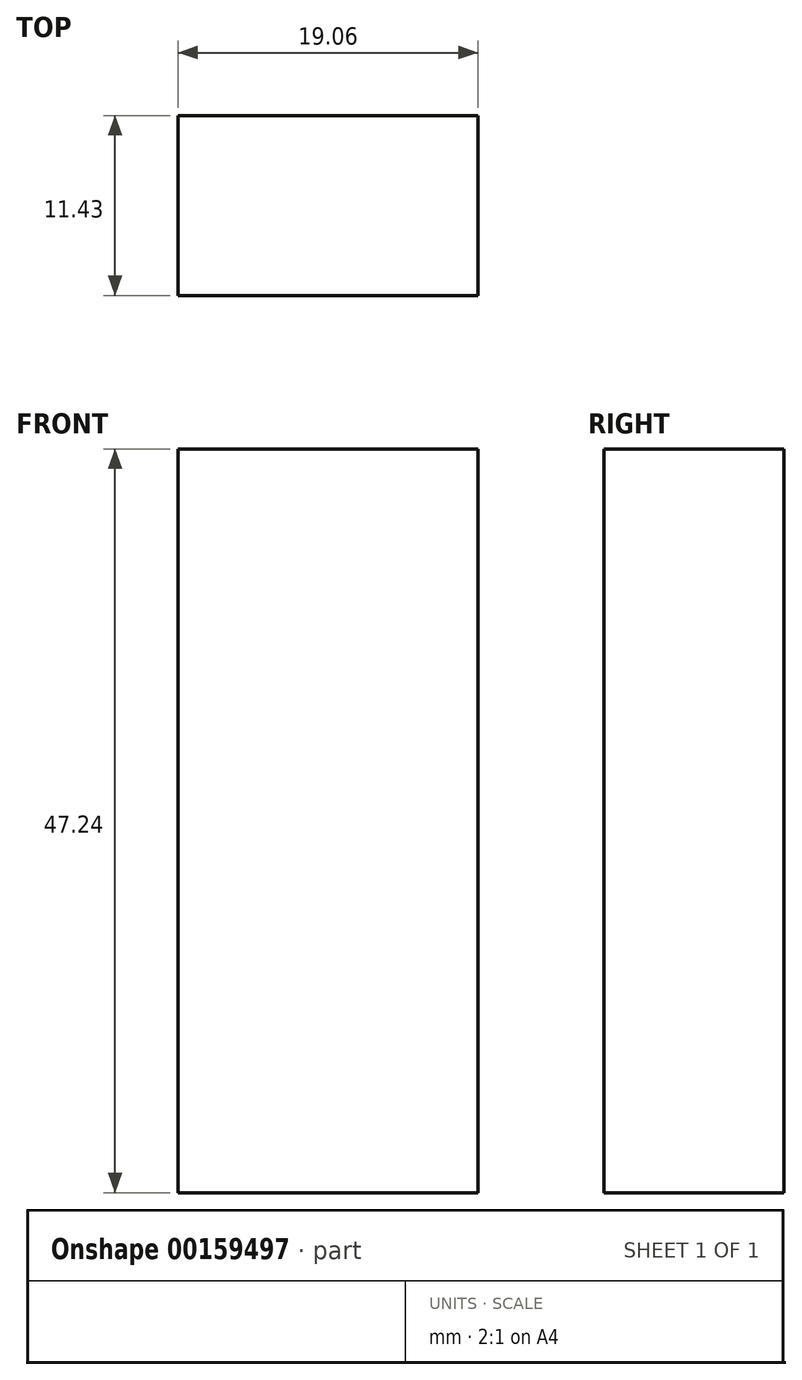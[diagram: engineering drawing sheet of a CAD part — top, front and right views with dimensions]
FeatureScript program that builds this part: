
annotation { "Feature Type Name" : "Feature", "Feature Type Description" : "" }
export const myFeature = defineFeature(function(context is Context, id is Id, definition is map)
    precondition{}
    {
        {
            var Q0;
            Q0=qCreatedBy(makeId("Front.planeOp"),FACE);
            var sketch = newSketch(context, id + "F0", { "sketchPlane" : qUnion([Q0])});
            skLineSegment(sketch, "E0.bottom", {"start": v(9.52, 23.62) * mm, "end": v(-9.53, 23.62) * mm});
            skLineSegment(sketch, "E0.top", {"start": v(9.53, -23.62) * mm, "end": v(-9.52, -23.62) * mm});
            skLineSegment(sketch, "E0.left", {"start": v(9.52, 23.62) * mm, "end": v(9.53, -23.62) * mm});
            skLineSegment(sketch, "E0.right", {"start": v(-9.53, 23.62) * mm, "end": v(-9.52, -23.62) * mm});
            skPoint(sketch, "E0.middle", {"position": v(0, 0) * mm});
            skSolve(sketch);
        }
        {
            var Q0;
            Q0 = qSketchRegion(id + "F0", true);
            extrude(context, id + "F1", {"entities" : qUnion([Q0]), "depth" : 15.24 * mm, "hasSecondDirection" : true, "secondDirectionOppositeDirection" : false, "secondDirectionDepth" : 3.8 * mm});
        }
    });
